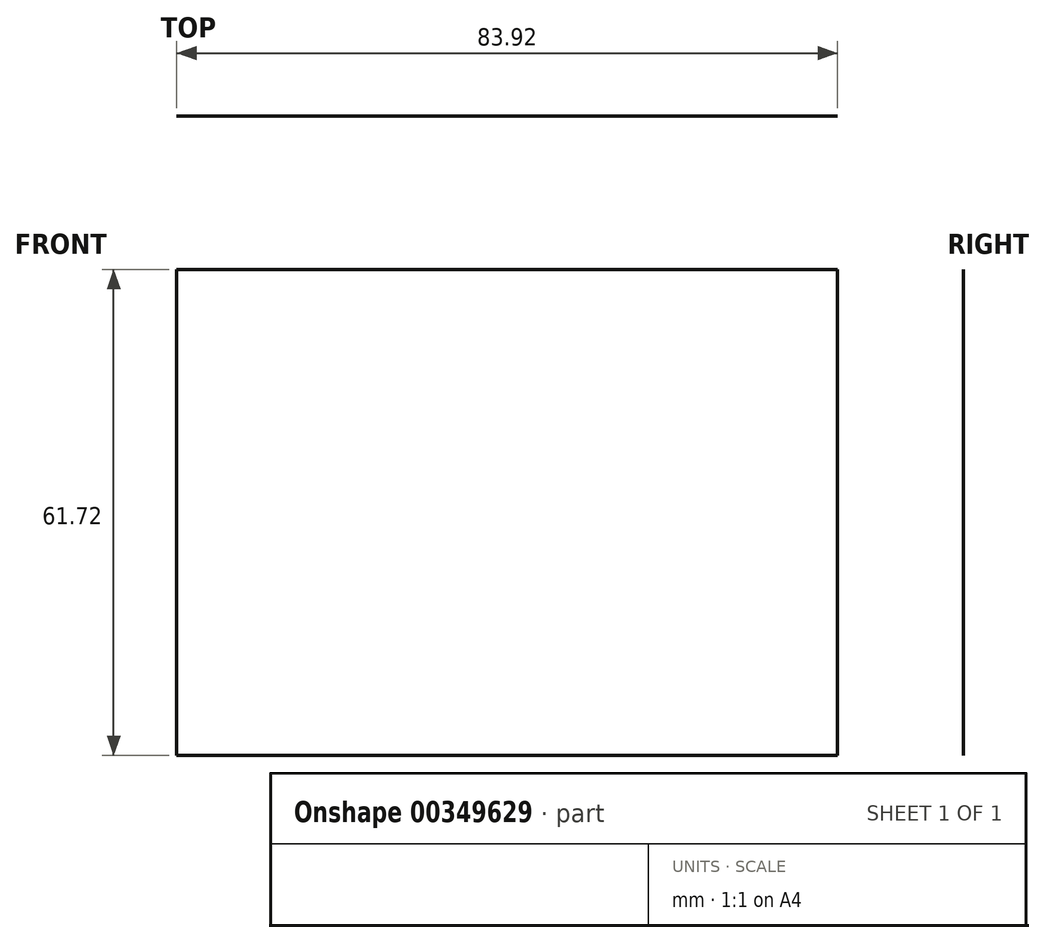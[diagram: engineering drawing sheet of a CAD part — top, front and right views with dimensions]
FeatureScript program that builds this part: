
annotation { "Feature Type Name" : "Feature", "Feature Type Description" : "" }
export const myFeature = defineFeature(function(context is Context, id is Id, definition is map)
    precondition{}
    {
        {
            var Q0;
            Q0=qCreatedBy(makeId("Top.planeOp"),FACE);
            var sketch = newSketch(context, id + "F0", { "sketchPlane" : qUnion([Q0])});
            skLineSegment(sketch, "E0.bottom", {"start": v(-107.59, 58.82) * mm, "end": v(-23.67, 58.82) * mm});
            skLineSegment(sketch, "E0.top", {"start": v(-107.59, 13.45) * mm, "end": v(-23.67, 13.45) * mm});
            skLineSegment(sketch, "E0.left", {"start": v(-107.59, 58.82) * mm, "end": v(-107.59, 13.45) * mm});
            skLineSegment(sketch, "E0.right", {"start": v(-23.67, 58.82) * mm, "end": v(-23.67, 13.45) * mm});
            skSolve(sketch);
        }
        {
            var Q0;
            Q0=sQuery(id+"F0.wireOp",EDGE,"E0.bottom");
            extrude(context, id + "F1", {"bodyType" : ToolBodyType.SURFACE, "surfaceEntities" : qUnion([Q0]), "depth" : 61.72 * mm});
        }
    });
